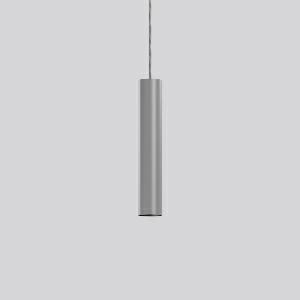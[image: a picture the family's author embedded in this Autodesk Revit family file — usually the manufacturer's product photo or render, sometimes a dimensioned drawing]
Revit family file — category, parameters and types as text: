
# Revit family: deecos_p_micro_911492_004_1_76_6fe4
name_source: partatom
category: Lighting Fixtures
units: mm (PartAtom-declared; Revit-internal decimal feet)

## family parameters
Cut with Voids When Loaded = No
Host = Face
Light Source = No
Part Type = Normal
Room Calculation Point = No
Round Connector Dimension = Use Diameter
Shared = No

## types (1)
- DEECOS P micro (1 x LED Modul 930, 1250 lm, 3000)
    Apparent Load = 16 VA
    CIE Flux Codes = 92 99 100 100 100
    Color Rendering = 90
    Color Temperature = 3000
    Default Elevation = 1800 mm
    Description = Series: DEECOS P micro
Cylindrical pendant luminaire. Housing: die-cast aluminium, powder-coated. Canopy made of powder-coated sheet steel with magnetic attachment. Optical assembly with lens made of plastic (polycarbonate) for the best homogeneous light distribution - can be changed without tools. Black plastic ring and recessed LED to prevent glare from the side. Best colour rendering index Ra>90. Transparent suspension cable 3 m, can be shortened. High quality converter without flickering and stroboscopic effect. 
Colour: silver
Diameter: 60 mm
Height: 340 mm
Suspension length: 3000 mm
Lamp: LED
Socket: without socket
Colour temperature: 3000K
Colour rendering index (CRI): 92
System power: 16 W
Rated luminous flux: 1250 lm
Luminous efficiency: 78 lm/W
Control gear: Converter, dimmable, DALI
Protection class: I
Type of protection: IP 20
    Height = 340 mm
    Lamp = 1 x LED Modul 930
    Lamp Light Flux = 1250 lm
    Lamp count = 1
    Length = 60 mm  [stored 0.19685 ft]
    Lifetime = 50000 h
    Luminous efficacy = 78 lm/W
    Manufacturer = RZB
    ModVariant = No
    Model = 911492.004.1.76
    Mounting Place = Ceiling
    Mounting Type = Pendant
    Number of Poles = 1
    OnlyDefault = Yes
    Power Factor = 1
    Product Name = DEECOS P micro
    Product group = Pendant luminaires
    ProductGroupID = 902
    Protection Class = Protection class I
    Protection Degree = Degree of protection
    RLX_Detail_Level = 1
    RLX_Emergency_Light_Flux = 0 lm
    RLX_Emergency_Type = 0
    RLX_Emergency_Type_DB = No
    RlxData = <blob elided: 31089 chars, md5=2c15b092>
    Socket = socket
    Standby Power = 0 W
    System Light Flux = 1250 lm
    System Power = 16 W
    Type Comments = Product without accessories
    Type Image = 911491.004.jpg
    URL = http://relux.com
    VarID = ---
    Voltage = 0 V
    Weight = 0.00 kg
    Width = 0 mm  [stored 0 ft]

note: [stored X ft] marks values corroborated as IEEE doubles in the binary element streams (Revit-internal decimal feet)

## geometry (parser evidence)
native form markers: Blend x4, Sweep x12
no freeform markers — native parametric forms only
